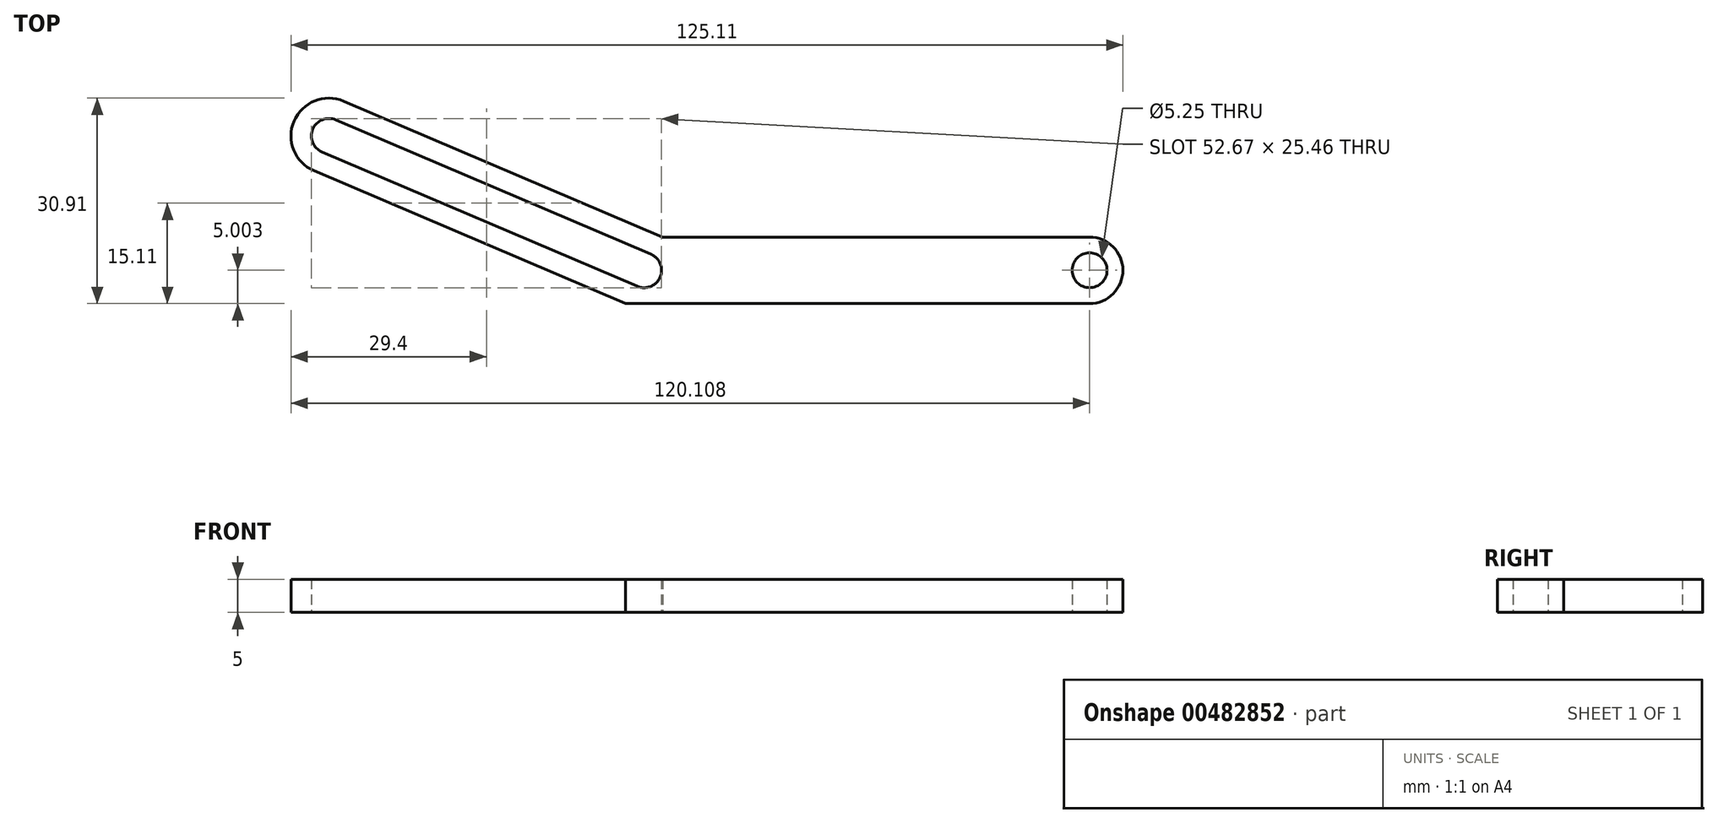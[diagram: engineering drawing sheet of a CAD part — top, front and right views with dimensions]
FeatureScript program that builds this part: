
annotation { "Feature Type Name" : "Feature", "Feature Type Description" : "" }
export const myFeature = defineFeature(function(context is Context, id is Id, definition is map)
    precondition{}
    {
        {
            var Q0;
            Q0=qCreatedBy(makeId("Top.planeOp"),FACE);
            var sketch = newSketch(context, id + "F0", { "sketchPlane" : qUnion([Q0])});
            skLineSegment(sketch, "E0", {"start": v(-49.81, 3.42) * mm, "end": v(17.19, 3.42) * mm});
            skLineSegment(sketch, "E1", {"start": v(17.19, 3.42) * mm, "end": v(17.19, 13.42) * mm});
            skLineSegment(sketch, "E2", {"start": v(17.19, 13.42) * mm, "end": v(-49.81, 13.42) * mm});
            skArc(sketch, "E3", {"start": v(17.19, 3.42) * mm, "mid": v(22.19, 8.42) * mm, "end": v(17.19, 13.42) * mm});
            skLineSegment(sketch, "E4", {"start": v(-49.81, 13.42) * mm, "end": v(-49.81, 3.42) * mm});
            skPoint(sketch, "E5", {"position": v(-49.81, 8.42) * mm});
            skCircle(sketch, "E6", {"center": v(-49.81, 8.42) * mm, "radius": 2.62 * mm});
            skCircle(sketch, "E7", {"center": v(17.19, 8.42) * mm, "radius": 2.62 * mm});
            skLineSegment(sketch, "E8", {"start": v(-52.6, 3.42) * mm, "end": v(-49.81, 3.42) * mm});
            skPoint(sketch, "E9", {"position": v(-47.03, 13.42) * mm});
            skLineSegment(sketch, "E10", {"start": v(-52.6, 3.42) * mm, "end": v(-99.46, 23.4) * mm});
            skLineSegment(sketch, "E11", {"start": v(-99.46, 23.4) * mm, "end": v(-95, 33.87) * mm});
            skLineSegment(sketch, "E12", {"start": v(-47.03, 13.42) * mm, "end": v(-95, 33.87) * mm});
            skArc(sketch, "E13", {"start": v(-95, 33.87) * mm, "mid": v(-102.46, 30.87) * mm, "end": v(-99.46, 23.4) * mm});
            skCircle(sketch, "E14", {"center": v(-97.23, 28.64) * mm, "radius": 2.62 * mm});
            skLineSegment(sketch, "E15", {"start": v(-96.2, 31.05) * mm, "end": v(-48.8, 10.85) * mm});
            skLineSegment(sketch, "E16", {"start": v(-98.26, 26.22) * mm, "end": v(-50.84, 6) * mm});
            skSolve(sketch);
        }
        {
            var Q0;
            {var subQ0=sQuery(id+"F0.wireOp",EDGE,"E3");Q0=makeQuery(id+"F0.imprint","IMPRINT",FACE,{"disambiguationData":[TD([[makeQuery(id+"F0.imprint","IMPRINT",EDGE,{"derivedFrom":subQ0}),1.0]])]});}
            var Q1;
            {var subQ13=sQuery(id+"F0.wireOp",EDGE,"E0");Q1=makeQuery(id+"F0.imprint","IMPRINT",FACE,{"disambiguationData":[TD([[makeQuery(id+"F0.imprint","IMPRINT",EDGE,{"derivedFrom":subQ13}),1.0]])]});}
            var Q2;
            {var subQ0=sQuery(id+"F0.wireOp",EDGE,"E12");Q2=makeQuery(id+"F0.imprint","IMPRINT",FACE,{"disambiguationData":[TD([[makeQuery(id+"F0.imprint","IMPRINT",EDGE,{"derivedFrom":subQ0}),1.0]])]});}
            var Q3;
            {var subQ0=sQuery(id+"F0.wireOp",EDGE,"E8");Q3=makeQuery(id+"F0.imprint","IMPRINT",FACE,{"disambiguationData":[TD([[makeQuery(id+"F0.imprint","IMPRINT",EDGE,{"derivedFrom":subQ0}),1.0]])]});}
            var Q4;
            {var subQ0=sQuery(id+"F0.wireOp",EDGE,"E13");Q4=makeQuery(id+"F0.imprint","IMPRINT",FACE,{"disambiguationData":[TD([[makeQuery(id+"F0.imprint","IMPRINT",EDGE,{"derivedFrom":subQ0}),1.0]])]});}
            extrude(context, id + "F1", {"entities" : qUnion([Q0, Q1, Q2, Q3, Q4]), "depth" : 5 * mm});
        }
    });
